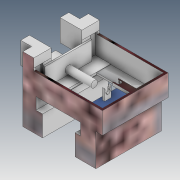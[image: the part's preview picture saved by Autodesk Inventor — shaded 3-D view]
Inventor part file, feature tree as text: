
AUTODESK INVENTOR PART (.ipt)
format: ipt  version: 2021 (Build 250183000, 183)  size: 633,856 bytes
history: native  units: in
note: dims shown in document units (in); Inventor stores cm internally (conversion verified against a paired STEP export)
features: extrude x34, sketch x34, fillet x2, other x1
ambient origin geometry x8: Origin, YZ Plane, XZ Plane, XY Plane, X Axis, Y Axis, Z Axis, Center Point
bodies: Body1 (feature_tree)
feature tree (71):
  other  "Sólido1"
  extrude  "Extrusão1"  Depth=0.1969in
  extrude  "Extrusão2"  Depth=0.3937in
  extrude  "Extrusão3"  Depth=0.0984in
  extrude  "Extrusão4"  Depth=0.3937in
  extrude  "Extrusão5"  Depth=0.3937in
  extrude  "Extrusão6"  Depth=0.0079in
  extrude  "Extrusão7"  Depth=0.0079in
  extrude  "Extrusão8"  Depth=0.0079in
  extrude  "Extrusão10"  Depth=0.0079in
  extrude  "Extrusão11"  Depth=0.0079in
  extrude  "Extrusão12"  Depth=0.0079in
  extrude  "Extrusão13"  Depth=0.0079in
  extrude  "Extrusão16"  Depth=0.0079in
  extrude  "Extrusão17"  Depth=0.2756in
  extrude  "Extrusão18"  Depth=0.0079in
  extrude  "Extrusão19"  Depth=0.0394in
  extrude  "Extrusão20"  Depth=0.0079in
  extrude  "Extrusão21"  Depth=0.0394in TaperAngle=0.0deg
  extrude  "Extrusão22"  Depth=0.3543in
  fillet  "Arredondamento1"  Radius=0.1969in
  extrude  "Extrusão23"  Depth=0.5394in TaperAngle=0.0deg
  extrude  "Extrusão24"  Depth=0.1969in TaperAngle=0.0deg
  fillet  "Arredondamento2"  Radius=0.0591in
  extrude  "Extrusão25"  Depth=0.2559in
  extrude  "Extrusão26"  Depth=0.0315in TaperAngle=0.0deg
  extrude  "Extrusão27"  Depth=0.0197in TaperAngle=0.0deg
  extrude  "Extrusão28"  Depth=0.0394in
  extrude  "Extrusão29"  Depth=0.0394in
  extrude  "Extrusão30"  Depth=0.0394in
  extrude  "Extrusão31"  Depth=0.0394in
  extrude  "Extrusão32"  Depth=0.0394in TaperAngle=0.0deg
  extrude  "Extrusão33"  Depth=0.0197in TaperAngle=0.0deg
  extrude  "Extrusão34"  Depth=0.0787in
  extrude  "Extrusão35"  Depth=0.0626in TaperAngle=0.0deg
  extrude  "Extrusão36"  Depth=0.1181in
  extrude  "Extrusão37"  Depth=0.0472in
  sketch  "Esboço2"  dims[d0=0.1969in d1=0.1969in]
  sketch  "Esboço4"  dims[d2=0.1181in d3=0.3937in]
  sketch  "Esboço5"  dims[d4=0.1969in d5=0.0984in]
  sketch  "Esboço6"  dims[d6=0.3937in d7=0.1969in]
  sketch  "Esboço7"  dims[d8=0.1969in d9=0.3937in]
  sketch  "Esboço8"  dims[d11=0.1969in d12=0.0079in]
  sketch  "Esboço10"  dims[d13=0.0079in d14=0.0079in]
  sketch  "Esboço12"  dims[d15=0.0079in d16=0.0079in]
  sketch  "Esboço15"  dims[d17=0.0079in d19=0.0079in]
  sketch  "Esboço16"  dims[d20=0.0079in d21=0.0079in]
  sketch  "Esboço18"  dims[d22=0.0079in d23=0.0079in]
  sketch  "Esboço20"  dims[d24=0.0079in d25=0.0079in]
  sketch  "Esboço23"  dims[d26=0.0079in d27=0.0079in]
  sketch  "Esboço25"  dims[d28=0.2756in d29=0.1575in]
  sketch  "Esboço26"  dims[d30=0.2756in d31=0.0079in]
  sketch  "Esboço28"  dims[d32=0.0787in d33=0.0394in]
  sketch  "Esboço29"  dims[d34=0.0079in d35=0.0787in]
  sketch  "Esboço30"  dims[d36=0.0394in d37=1.1811in d38=0.0in]
  sketch  "Esboço32"  dims[d39=0.4724in d40=0.3543in d46=0.1969in d47=0.0in]
  sketch  "Esboço33"  dims[d48=0.1181in d49=0.5394in d50=0.0in]
  sketch  "Esboço34"  dims[d51=0.1969in d52=0.0in d53=0.1969in d54=0.0in d55=0.0591in]
  sketch  "Esboço38"  dims[d56=0.1969in d57=0.0in d58=0.2559in]
  sketch  "Esboço39"  dims[d59=0.2559in d60=0.0315in d61=0.0in]
  sketch  "Esboço40"  dims[d62=0.1575in d63=0.0197in d64=0.0in]
  sketch  "Esboço41"  dims[d68=0.1181in d69=0.0in d70=0.0394in]
  sketch  "Esboço42"  dims[d71=0.0394in d73=0.0394in]
  sketch  "Esboço43"  dims[d74=0.3937in d75=0.0in d76=0.0394in]
  sketch  "Esboço44"  dims[d77=0.0in d78=0.0in d79=0.0394in]
  sketch  "Esboço45"  dims[d80=0.0394in d81=0.0394in d82=0.0in]
  sketch  "Esboço46"  dims[d91=0.4134in d92=0.0197in d93=0.0in]
  sketch  "Esboço47"  dims[d94=0.0157in d95=0.0in d96=0.0787in]
  sketch  "Esboço48"  dims[d97=0.0787in d98=0.0626in d99=0.0in]
  sketch  "Esboço50"  dims[d100=0.0197in d101=0.0in d102=0.1181in]
  sketch  "Esboço51"  dims[d103=0.0197in d104=0.0in d105=0.0591in d106=0.0591in d107=0.0591in d108=0.1969in d109=0.0in d110=0.0787in d111=0.0394in d112=0.0787in d114=0.0394in d115=0.0in d116=0.0394in d117=0.0591in d118=0.0591in d119=0.0984in d120=0.3543in d121=0.0in d123=0.0803in d124=0.0984in d125=0.0in d126=0.0079in d128=0.7874in d129=0.1969in d130=0.1969in d131=0.1181in d132=0.3937in d133=0.1969in d134=0.1181in d135=0.1181in d136=0.1969in d137=0.0in d138=0.0039in d139=0.0433in d140=0.0039in d141=0.3858in d142=0.0in d143=0.3937in d144=0.0in d147=0.3858in d148=0.0in d149=0.2283in d150=0.2283in d151=0.0591in d152=0.0in d153=0.0591in d154=0.0in d155=0.1969in d156=0.0in d157=0.3937in d158=0.1969in d159=0.0in d160=0.1969in d161=0.0in d163=0.1575in d164=0.1969in d165=0.0in d166=0.1969in d167=0.0in d170=0.374in d171=0.0in d172=0.7874in d173=0.0472in d174=0.0in d168=0.0197in d169=0.0344in]
